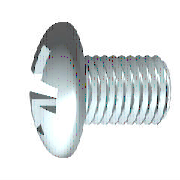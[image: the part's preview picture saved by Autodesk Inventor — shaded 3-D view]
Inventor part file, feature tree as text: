
AUTODESK INVENTOR PART (.ipt)
format: ipt  version: 2024 (Build 280153000, 153)  size: 258,560 bytes
history: native  units: mm (DEFAULTED — no unit token found)
features: extrude x1, other x1, plane x1
ambient origin geometry x7: Origin, YZ Plane, XZ Plane, X Axis, Y Axis, Z Axis, Center Point
bodies: Solid1 (feature_tree), Body (feature_tree)
feature tree (3):
  extrude  "Slot"  Depth=3.0mm
  other  "Cut"
  plane  "Work Plane3"
